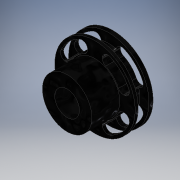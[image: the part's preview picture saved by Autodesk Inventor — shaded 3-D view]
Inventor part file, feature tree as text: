
AUTODESK INVENTOR PART (.ipt)
format: ipt  version: 2019.4 (Build 234330000, 330)  size: 307,712 bytes
history: native  units: mm
features: sketch x8, extrude x7, pattern_circular x3, projected_geometry x3, fillet x2, hole x1
ambient origin geometry x8: Origin, YZ Plane, XZ Plane, XY Plane, X Axis, Y Axis, Z Axis, Center Point
bodies: Solid1 (feature_tree)
feature tree (24):
  extrude  "Extrusion1"  Depth=12.0mm
  extrude  "Extrusion2"  Depth=4.0mm TaperAngle=0.0deg
  extrude  "Extrusion3"  Depth=1.5mm TaperAngle=0.0deg
  extrude  "Extrusion4"  Depth=5.2mm TaperAngle=0.0deg
  extrude  "Extrusion5"  Depth=2.0mm
  extrude  "Extrusion6"  Depth=1.8mm
  fillet  "Fillet1"  Radius=0.9mm
  pattern_circular  "Circular Pattern1"  Count=4 Angle=360.0deg
  hole  "Hole1"  [1 undecoded]
  pattern_circular  "Circular Pattern2"  Count=4 Angle=360.0deg
  extrude  "Extrusion7"  Depth=2.6mm
  fillet  "Fillet2"  Radius=40.0mm
  pattern_circular  "Circular Pattern3"  [2 undecoded]
  sketch  "Sketch1"  dims[d0=24.0mm d1=12.0mm]
  sketch  "Sketch2"  dims[d2=10.0mm d3=0.0mm d4=4.0mm d5=0.0mm]
  projected_geometry  "Projected Loop1"
  sketch  "Sketch3"  dims[d6=39.0mm d7=1.5mm d8=0.0mm]
  sketch  "Sketch4"  dims[d9=30.0mm d10=5.2mm d11=0.0mm]
  projected_geometry  "Projected Loop2"
  sketch  "Sketch5"  dims[d12=2.0mm d13=0.0mm d14=14.2mm]
  sketch  "Sketch6"  dims[d15=21.2mm d16=1.8mm d17=0.9mm d18=40.0mm d20=360.0deg]
  sketch  "Sketch7"  dims[d22=7.0mm d23=0.0mm d24=1.7mm d25=40.0mm d26=360.0deg]
  sketch  "Sketch8"  dims[d28=25.0mm d29=3.0mm d30=2.459mm d31=6.0mm d32=4.0mm d33=2.0mm d34=90.0deg d35=8.0mm d36=0.0mm d37=40.0mm d38=360.0deg d40=25.0mm d41=36.0mm d42=7.3mm d43=3.65mm d44=40.0mm d46=360.0deg d48=2.0mm d49=0.0mm d50=2.6mm d51=40.0mm d52=360.0deg]
  projected_geometry  "Projected Loop3"
note: 3 required parameter values undecoded (feature->parameter linkage not recoverable at this tier; creation-order binding heuristic only, values carry confidence <= 0.55)
